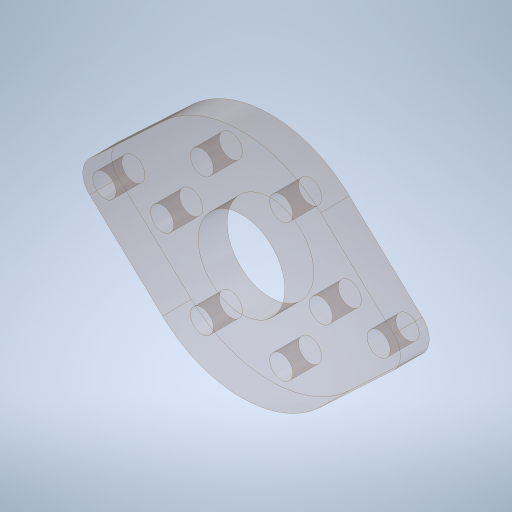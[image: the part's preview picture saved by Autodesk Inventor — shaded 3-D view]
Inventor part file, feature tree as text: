
AUTODESK INVENTOR PART (.ipt)
format: ipt  version: 2023.4 (Build 274418000, 418)  size: 301,568 bytes
history: native  units: in
note: dims shown in document units (in); Inventor stores cm internally (conversion verified against a paired STEP export)
features: sketch x1, extrude x1, hole x1
ambient origin geometry x8: Origin, YZ Plane, XZ Plane, XY Plane, X Axis, Y Axis, Z Axis, Center Point
bodies: Solid1 (feature_tree)
feature tree (3):
  sketch  "Sketch1"  dims[d0=0.75in d1=2.0in d2=0.375in d3=1.375in d4=2.3622in d6=360.0deg d8=0.25in d9=0.0in d10=0.201in d11=0.75in d12=0.385in d13=0.25in d14=0.5635in d15=1.0in d16=0.8108in]
  extrude  "Extrusion1"  Depth=2.0in
  hole  "Hole1"  [1 undecoded]
note: 1 required parameter value undecoded (feature->parameter linkage not recoverable at this tier; creation-order binding heuristic only, values carry confidence <= 0.55)
